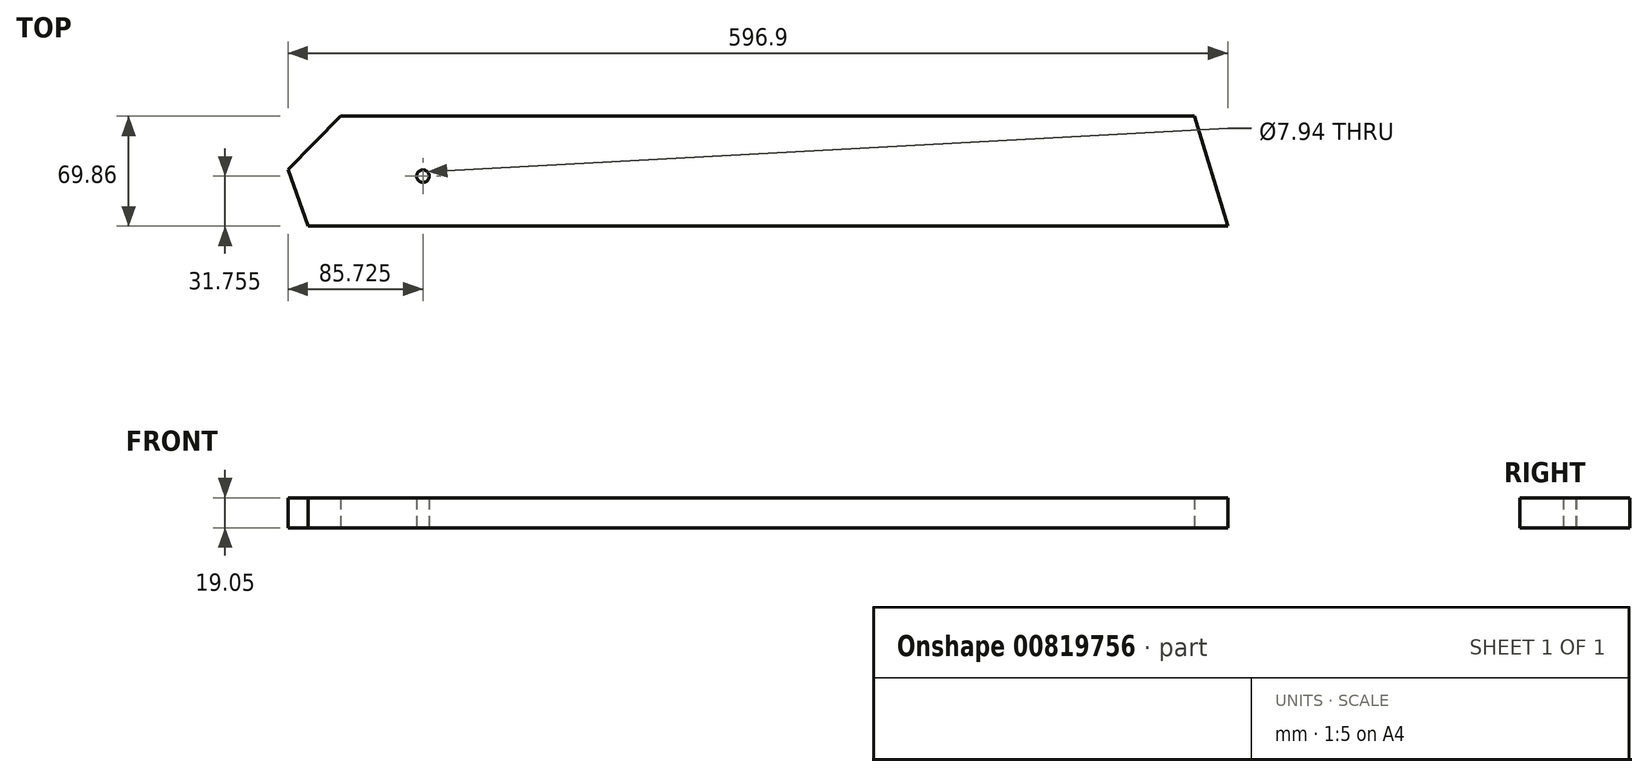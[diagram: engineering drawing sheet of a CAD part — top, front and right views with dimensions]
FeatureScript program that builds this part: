
annotation { "Feature Type Name" : "Feature", "Feature Type Description" : "" }
export const myFeature = defineFeature(function(context is Context, id is Id, definition is map)
    precondition{}
    {
        {
            var Q0;
            Q0=qCreatedBy(makeId("Top.planeOp"),FACE);
            var sketch = newSketch(context, id + "F0", { "sketchPlane" : qUnion([Q0])});
            skLineSegment(sketch, "E0.bottom", {"start": v(277.15, 34.93) * mm, "end": v(-265.03, 34.93) * mm});
            skLineSegment(sketch, "E0.top", {"start": v(298.45, -34.93) * mm, "end": v(-285.75, -34.93) * mm});
            skPoint(sketch, "E0.middle", {"position": v(0, 0) * mm});
            skLineSegment(sketch, "E1", {"start": v(-285.75, 34.93) * mm, "end": v(-285.75, -34.93) * mm, "construction": true});
            skLineSegment(sketch, "E2", {"start": v(-285.75, -34.92) * mm, "end": v(-298.45, 1) * mm, "construction": true});
            skLineSegment(sketch, "E3", {"start": v(-298.45, 1) * mm, "end": v(-285.75, -34.92) * mm});
            skLineSegment(sketch, "E4", {"start": v(-298.45, 1) * mm, "end": v(-265.03, 34.93) * mm, "construction": true});
            skLineSegment(sketch, "E5", {"start": v(-298.45, 1) * mm, "end": v(-265.03, 34.93) * mm});
            skLineSegment(sketch, "E6", {"start": v(298.45, -34.93) * mm, "end": v(277.15, 34.93) * mm, "construction": true});
            skLineSegment(sketch, "E7", {"start": v(277.15, 34.93) * mm, "end": v(298.45, -34.93) * mm});
            skLineSegment(sketch, "E8", {"start": v(-298.45, -3.18) * mm, "end": v(298.45, -3.18) * mm, "construction": true});
            skLineSegment(sketch, "E9", {"start": v(-212.73, 34.93) * mm, "end": v(-212.73, -34.93) * mm, "construction": true});
            skCircle(sketch, "E10", {"center": v(-212.73, -3.18) * mm, "radius": 3.97 * mm});
            skPoint(sketch, "E11.orphan", {"position": v(-298.45, 34.93) * mm});
            skPoint(sketch, "E12.orphan", {"position": v(-298.45, -34.93) * mm});
            skPoint(sketch, "E13.orphan", {"position": v(298.45, 34.93) * mm});
            skSolve(sketch);
        }
        {
            var Q0;
            Q0=makeQuery(id+"F0.imprint","IMPRINT",FACE,{"disambiguationData":[TD([[makeQuery(id+"F0.imprint","IMPRINT",EDGE,{"derivedFrom":sQuery(id+"F0.wireOp",EDGE,"E0.bottom")}),1.0]])]});
            extrude(context, id + "F1", {"entities" : qUnion([Q0]), "depth" : 19.05 * mm, "offsetDistance" : 25.4 * mm});
        }
    });
